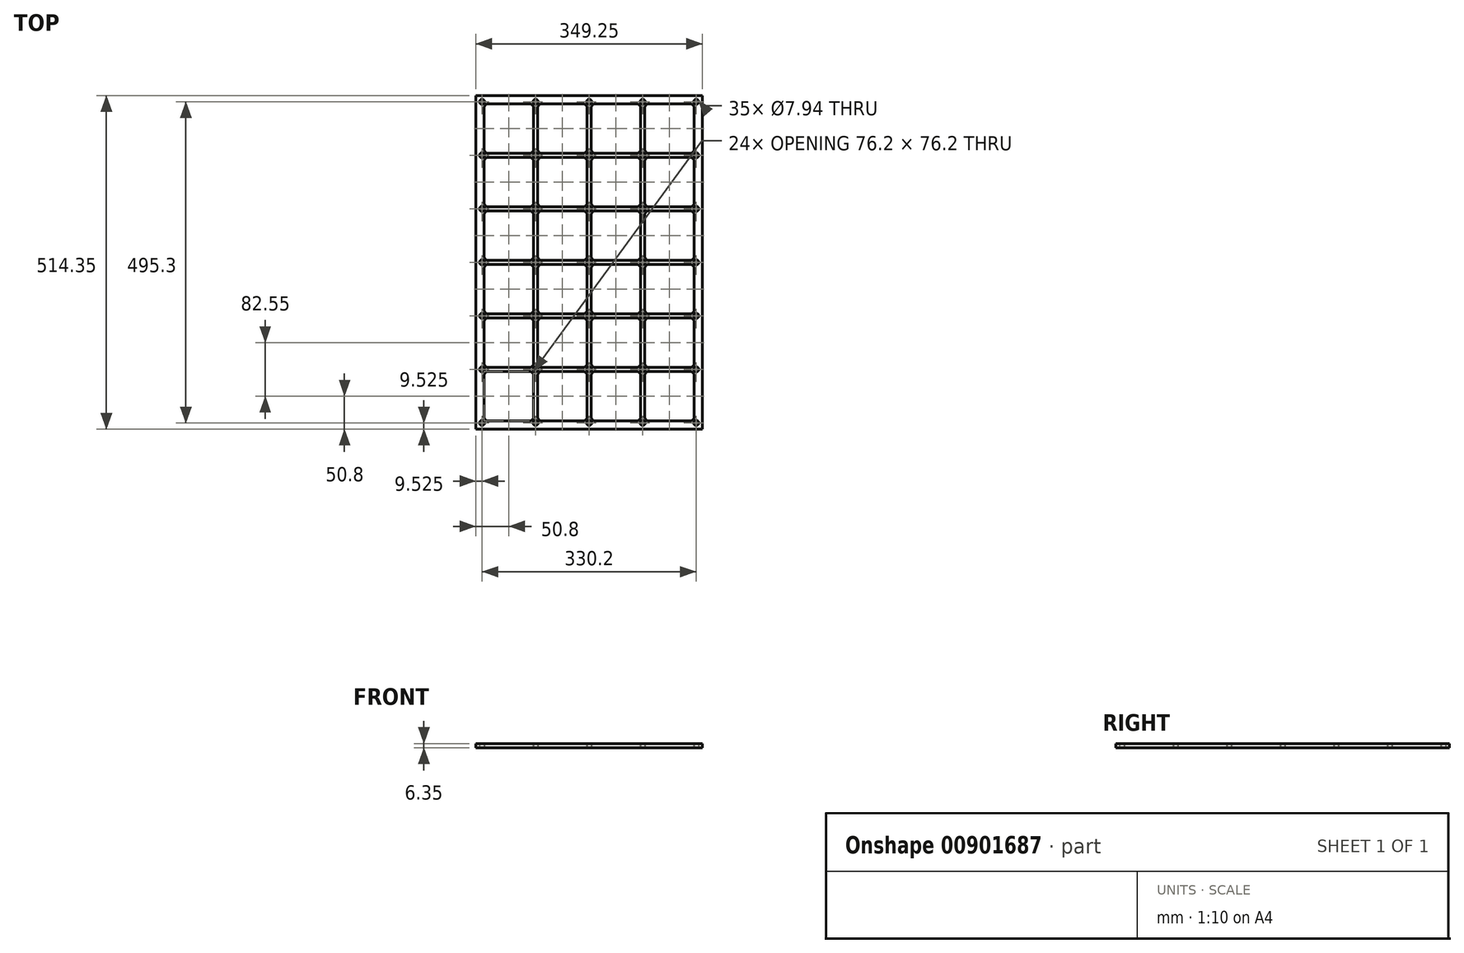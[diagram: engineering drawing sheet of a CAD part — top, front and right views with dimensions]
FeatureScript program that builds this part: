
annotation { "Feature Type Name" : "Feature", "Feature Type Description" : "" }
export const myFeature = defineFeature(function(context is Context, id is Id, definition is map)
    precondition{}
    {
        {
            var Q0;
            Q0=qCreatedBy(makeId("Top.planeOp"),FACE);
            var sketch = newSketch(context, id + "F0", { "sketchPlane" : qUnion([Q0])});
            skLineSegment(sketch, "E0.bottom", {"start": v(0, 0) * mm, "end": v(349.25, 0) * mm});
            skLineSegment(sketch, "E0.top", {"start": v(0, 514.35) * mm, "end": v(349.25, 514.35) * mm});
            skLineSegment(sketch, "E0.left", {"start": v(0, 0) * mm, "end": v(0, 514.35) * mm});
            skLineSegment(sketch, "E0.right", {"start": v(349.25, 0) * mm, "end": v(349.25, 514.35) * mm});
            skLineSegment(sketch, "E1.bottom", {"start": v(19.05, 12.7) * mm, "end": v(82.55, 12.7) * mm});
            skLineSegment(sketch, "E1.top", {"start": v(19.05, 88.9) * mm, "end": v(82.55, 88.9) * mm});
            skLineSegment(sketch, "E1.left", {"start": v(12.7, 19.05) * mm, "end": v(12.7, 82.55) * mm});
            skLineSegment(sketch, "E1.right", {"start": v(88.9, 19.05) * mm, "end": v(88.9, 82.55) * mm});
            skArc(sketch, "E2.filletArc", {"start": v(19.05, 88.9) * mm, "mid": v(14.56, 87.04) * mm, "end": v(12.7, 82.55) * mm});
            skArc(sketch, "E3.filletArc", {"start": v(88.9, 82.55) * mm, "mid": v(87.04, 87.04) * mm, "end": v(82.55, 88.9) * mm});
            skArc(sketch, "E4.filletArc", {"start": v(82.55, 12.7) * mm, "mid": v(87.04, 14.56) * mm, "end": v(88.9, 19.05) * mm});
            skArc(sketch, "E5.filletArc", {"start": v(12.7, 19.05) * mm, "mid": v(14.56, 14.56) * mm, "end": v(19.05, 12.7) * mm});
            skLineSegment(sketch, "E6.0.1.0", {"start": v(19.05, 171.45) * mm, "end": v(82.55, 171.45) * mm});
            skLineSegment(sketch, "E6.0.1.1", {"start": v(88.9, 101.6) * mm, "end": v(88.9, 165.1) * mm});
            skArc(sketch, "E6.0.1.2", {"start": v(88.9, 165.1) * mm, "mid": v(87.04, 169.6) * mm, "end": v(82.55, 171.45) * mm});
            skArc(sketch, "E6.0.1.3", {"start": v(82.55, 95.25) * mm, "mid": v(87.04, 97.1) * mm, "end": v(88.9, 101.6) * mm});
            skLineSegment(sketch, "E6.0.1.4", {"start": v(19.05, 95.25) * mm, "end": v(82.55, 95.25) * mm});
            skArc(sketch, "E6.0.1.5", {"start": v(12.7, 101.6) * mm, "mid": v(14.56, 97.1) * mm, "end": v(19.05, 95.25) * mm});
            skLineSegment(sketch, "E6.0.1.6", {"start": v(12.7, 101.6) * mm, "end": v(12.7, 165.1) * mm});
            skArc(sketch, "E6.0.1.7", {"start": v(19.05, 171.45) * mm, "mid": v(14.56, 169.6) * mm, "end": v(12.7, 165.1) * mm});
            skLineSegment(sketch, "E6.0.2.0", {"start": v(19.05, 254) * mm, "end": v(82.55, 254) * mm});
            skLineSegment(sketch, "E6.0.2.1", {"start": v(88.9, 184.15) * mm, "end": v(88.9, 247.65) * mm});
            skArc(sketch, "E6.0.2.2", {"start": v(88.9, 247.65) * mm, "mid": v(87.04, 252.14) * mm, "end": v(82.55, 254) * mm});
            skArc(sketch, "E6.0.2.3", {"start": v(82.55, 177.8) * mm, "mid": v(87.04, 179.66) * mm, "end": v(88.9, 184.15) * mm});
            skLineSegment(sketch, "E6.0.2.4", {"start": v(19.05, 177.8) * mm, "end": v(82.55, 177.8) * mm});
            skArc(sketch, "E6.0.2.5", {"start": v(12.7, 184.15) * mm, "mid": v(14.56, 179.66) * mm, "end": v(19.05, 177.8) * mm});
            skLineSegment(sketch, "E6.0.2.6", {"start": v(12.7, 184.15) * mm, "end": v(12.7, 247.65) * mm});
            skArc(sketch, "E6.0.2.7", {"start": v(19.05, 254) * mm, "mid": v(14.56, 252.14) * mm, "end": v(12.7, 247.65) * mm});
            skLineSegment(sketch, "E6.0.3.0", {"start": v(19.05, 336.55) * mm, "end": v(82.55, 336.55) * mm});
            skLineSegment(sketch, "E6.0.3.1", {"start": v(88.9, 266.7) * mm, "end": v(88.9, 330.2) * mm});
            skArc(sketch, "E6.0.3.2", {"start": v(88.9, 330.2) * mm, "mid": v(87.04, 334.7) * mm, "end": v(82.55, 336.55) * mm});
            skArc(sketch, "E6.0.3.3", {"start": v(82.55, 260.35) * mm, "mid": v(87.04, 262.2) * mm, "end": v(88.9, 266.7) * mm});
            skLineSegment(sketch, "E6.0.3.4", {"start": v(19.05, 260.35) * mm, "end": v(82.55, 260.35) * mm});
            skArc(sketch, "E6.0.3.5", {"start": v(12.7, 266.7) * mm, "mid": v(14.56, 262.2) * mm, "end": v(19.05, 260.35) * mm});
            skLineSegment(sketch, "E6.0.3.6", {"start": v(12.7, 266.7) * mm, "end": v(12.7, 330.2) * mm});
            skArc(sketch, "E6.0.3.7", {"start": v(19.05, 336.55) * mm, "mid": v(14.56, 334.7) * mm, "end": v(12.7, 330.2) * mm});
            skLineSegment(sketch, "E6.0.4.0", {"start": v(19.05, 419.1) * mm, "end": v(82.55, 419.1) * mm});
            skLineSegment(sketch, "E6.0.4.1", {"start": v(88.9, 349.25) * mm, "end": v(88.9, 412.75) * mm});
            skArc(sketch, "E6.0.4.2", {"start": v(88.9, 412.75) * mm, "mid": v(87.04, 417.24) * mm, "end": v(82.55, 419.1) * mm});
            skArc(sketch, "E6.0.4.3", {"start": v(82.55, 342.9) * mm, "mid": v(87.04, 344.76) * mm, "end": v(88.9, 349.25) * mm});
            skLineSegment(sketch, "E6.0.4.4", {"start": v(19.05, 342.9) * mm, "end": v(82.55, 342.9) * mm});
            skArc(sketch, "E6.0.4.5", {"start": v(12.7, 349.25) * mm, "mid": v(14.56, 344.76) * mm, "end": v(19.05, 342.9) * mm});
            skLineSegment(sketch, "E6.0.4.6", {"start": v(12.7, 349.25) * mm, "end": v(12.7, 412.75) * mm});
            skArc(sketch, "E6.0.4.7", {"start": v(19.05, 419.1) * mm, "mid": v(14.56, 417.24) * mm, "end": v(12.7, 412.75) * mm});
            skLineSegment(sketch, "E6.0.5.0", {"start": v(19.05, 501.65) * mm, "end": v(82.55, 501.65) * mm});
            skLineSegment(sketch, "E6.0.5.1", {"start": v(88.9, 431.8) * mm, "end": v(88.9, 495.3) * mm});
            skArc(sketch, "E6.0.5.2", {"start": v(88.9, 495.3) * mm, "mid": v(87.04, 499.8) * mm, "end": v(82.55, 501.65) * mm});
            skArc(sketch, "E6.0.5.3", {"start": v(82.55, 425.45) * mm, "mid": v(87.04, 427.3) * mm, "end": v(88.9, 431.8) * mm});
            skLineSegment(sketch, "E6.0.5.4", {"start": v(19.05, 425.45) * mm, "end": v(82.55, 425.45) * mm});
            skArc(sketch, "E6.0.5.5", {"start": v(12.7, 431.8) * mm, "mid": v(14.56, 427.3) * mm, "end": v(19.05, 425.45) * mm});
            skLineSegment(sketch, "E6.0.5.6", {"start": v(12.7, 431.8) * mm, "end": v(12.7, 495.3) * mm});
            skArc(sketch, "E6.0.5.7", {"start": v(19.05, 501.65) * mm, "mid": v(14.56, 499.8) * mm, "end": v(12.7, 495.3) * mm});
            skLineSegment(sketch, "E6.1.0.0", {"start": v(101.6, 88.9) * mm, "end": v(165.1, 88.9) * mm});
            skLineSegment(sketch, "E6.1.0.1", {"start": v(171.45, 19.05) * mm, "end": v(171.45, 82.55) * mm});
            skArc(sketch, "E6.1.0.2", {"start": v(171.45, 82.55) * mm, "mid": v(169.6, 87.04) * mm, "end": v(165.1, 88.9) * mm});
            skArc(sketch, "E6.1.0.3", {"start": v(165.1, 12.7) * mm, "mid": v(169.6, 14.56) * mm, "end": v(171.45, 19.05) * mm});
            skLineSegment(sketch, "E6.1.0.4", {"start": v(101.6, 12.7) * mm, "end": v(165.1, 12.7) * mm});
            skArc(sketch, "E6.1.0.5", {"start": v(95.25, 19.05) * mm, "mid": v(97.1, 14.56) * mm, "end": v(101.6, 12.7) * mm});
            skLineSegment(sketch, "E6.1.0.6", {"start": v(95.25, 19.05) * mm, "end": v(95.25, 82.55) * mm});
            skArc(sketch, "E6.1.0.7", {"start": v(101.6, 88.9) * mm, "mid": v(97.1, 87.04) * mm, "end": v(95.25, 82.55) * mm});
            skLineSegment(sketch, "E6.1.1.0", {"start": v(101.6, 171.45) * mm, "end": v(165.1, 171.45) * mm});
            skLineSegment(sketch, "E6.1.1.1", {"start": v(171.45, 101.6) * mm, "end": v(171.45, 165.1) * mm});
            skArc(sketch, "E6.1.1.2", {"start": v(171.45, 165.1) * mm, "mid": v(169.6, 169.6) * mm, "end": v(165.1, 171.45) * mm});
            skArc(sketch, "E6.1.1.3", {"start": v(165.1, 95.25) * mm, "mid": v(169.6, 97.1) * mm, "end": v(171.45, 101.6) * mm});
            skLineSegment(sketch, "E6.1.1.4", {"start": v(101.6, 95.25) * mm, "end": v(165.1, 95.25) * mm});
            skArc(sketch, "E6.1.1.5", {"start": v(95.25, 101.6) * mm, "mid": v(97.1, 97.1) * mm, "end": v(101.6, 95.25) * mm});
            skLineSegment(sketch, "E6.1.1.6", {"start": v(95.25, 101.6) * mm, "end": v(95.25, 165.1) * mm});
            skArc(sketch, "E6.1.1.7", {"start": v(101.6, 171.45) * mm, "mid": v(97.1, 169.6) * mm, "end": v(95.25, 165.1) * mm});
            skLineSegment(sketch, "E6.1.2.0", {"start": v(101.6, 254) * mm, "end": v(165.1, 254) * mm});
            skLineSegment(sketch, "E6.1.2.1", {"start": v(171.45, 184.15) * mm, "end": v(171.45, 247.65) * mm});
            skArc(sketch, "E6.1.2.2", {"start": v(171.45, 247.65) * mm, "mid": v(169.6, 252.14) * mm, "end": v(165.1, 254) * mm});
            skArc(sketch, "E6.1.2.3", {"start": v(165.1, 177.8) * mm, "mid": v(169.6, 179.66) * mm, "end": v(171.45, 184.15) * mm});
            skLineSegment(sketch, "E6.1.2.4", {"start": v(101.6, 177.8) * mm, "end": v(165.1, 177.8) * mm});
            skArc(sketch, "E6.1.2.5", {"start": v(95.25, 184.15) * mm, "mid": v(97.1, 179.66) * mm, "end": v(101.6, 177.8) * mm});
            skLineSegment(sketch, "E6.1.2.6", {"start": v(95.25, 184.15) * mm, "end": v(95.25, 247.65) * mm});
            skArc(sketch, "E6.1.2.7", {"start": v(101.6, 254) * mm, "mid": v(97.1, 252.14) * mm, "end": v(95.25, 247.65) * mm});
            skLineSegment(sketch, "E6.1.3.0", {"start": v(101.6, 336.55) * mm, "end": v(165.1, 336.55) * mm});
            skLineSegment(sketch, "E6.1.3.1", {"start": v(171.45, 266.7) * mm, "end": v(171.45, 330.2) * mm});
            skArc(sketch, "E6.1.3.2", {"start": v(171.45, 330.2) * mm, "mid": v(169.6, 334.7) * mm, "end": v(165.1, 336.55) * mm});
            skArc(sketch, "E6.1.3.3", {"start": v(165.1, 260.35) * mm, "mid": v(169.6, 262.2) * mm, "end": v(171.45, 266.7) * mm});
            skLineSegment(sketch, "E6.1.3.4", {"start": v(101.6, 260.35) * mm, "end": v(165.1, 260.35) * mm});
            skArc(sketch, "E6.1.3.5", {"start": v(95.25, 266.7) * mm, "mid": v(97.1, 262.2) * mm, "end": v(101.6, 260.35) * mm});
            skLineSegment(sketch, "E6.1.3.6", {"start": v(95.25, 266.7) * mm, "end": v(95.25, 330.2) * mm});
            skArc(sketch, "E6.1.3.7", {"start": v(101.6, 336.55) * mm, "mid": v(97.1, 334.7) * mm, "end": v(95.25, 330.2) * mm});
            skLineSegment(sketch, "E6.1.4.0", {"start": v(101.6, 419.1) * mm, "end": v(165.1, 419.1) * mm});
            skLineSegment(sketch, "E6.1.4.1", {"start": v(171.45, 349.25) * mm, "end": v(171.45, 412.75) * mm});
            skArc(sketch, "E6.1.4.2", {"start": v(171.45, 412.75) * mm, "mid": v(169.6, 417.24) * mm, "end": v(165.1, 419.1) * mm});
            skArc(sketch, "E6.1.4.3", {"start": v(165.1, 342.9) * mm, "mid": v(169.6, 344.76) * mm, "end": v(171.45, 349.25) * mm});
            skLineSegment(sketch, "E6.1.4.4", {"start": v(101.6, 342.9) * mm, "end": v(165.1, 342.9) * mm});
            skArc(sketch, "E6.1.4.5", {"start": v(95.25, 349.25) * mm, "mid": v(97.1, 344.76) * mm, "end": v(101.6, 342.9) * mm});
            skLineSegment(sketch, "E6.1.4.6", {"start": v(95.25, 349.25) * mm, "end": v(95.25, 412.75) * mm});
            skArc(sketch, "E6.1.4.7", {"start": v(101.6, 419.1) * mm, "mid": v(97.1, 417.24) * mm, "end": v(95.25, 412.75) * mm});
            skLineSegment(sketch, "E6.1.5.0", {"start": v(101.6, 501.65) * mm, "end": v(165.1, 501.65) * mm});
            skLineSegment(sketch, "E6.1.5.1", {"start": v(171.45, 431.8) * mm, "end": v(171.45, 495.3) * mm});
            skArc(sketch, "E6.1.5.2", {"start": v(171.45, 495.3) * mm, "mid": v(169.6, 499.8) * mm, "end": v(165.1, 501.65) * mm});
            skArc(sketch, "E6.1.5.3", {"start": v(165.1, 425.45) * mm, "mid": v(169.6, 427.3) * mm, "end": v(171.45, 431.8) * mm});
            skLineSegment(sketch, "E6.1.5.4", {"start": v(101.6, 425.45) * mm, "end": v(165.1, 425.45) * mm});
            skArc(sketch, "E6.1.5.5", {"start": v(95.25, 431.8) * mm, "mid": v(97.1, 427.3) * mm, "end": v(101.6, 425.45) * mm});
            skLineSegment(sketch, "E6.1.5.6", {"start": v(95.25, 431.8) * mm, "end": v(95.25, 495.3) * mm});
            skArc(sketch, "E6.1.5.7", {"start": v(101.6, 501.65) * mm, "mid": v(97.1, 499.8) * mm, "end": v(95.25, 495.3) * mm});
            skLineSegment(sketch, "E6.2.0.0", {"start": v(184.15, 88.9) * mm, "end": v(247.65, 88.9) * mm});
            skLineSegment(sketch, "E6.2.0.1", {"start": v(254, 19.05) * mm, "end": v(254, 82.55) * mm});
            skArc(sketch, "E6.2.0.2", {"start": v(254, 82.55) * mm, "mid": v(252.14, 87.04) * mm, "end": v(247.65, 88.9) * mm});
            skArc(sketch, "E6.2.0.3", {"start": v(247.65, 12.7) * mm, "mid": v(252.14, 14.56) * mm, "end": v(254, 19.05) * mm});
            skLineSegment(sketch, "E6.2.0.4", {"start": v(184.15, 12.7) * mm, "end": v(247.65, 12.7) * mm});
            skArc(sketch, "E6.2.0.5", {"start": v(177.8, 19.05) * mm, "mid": v(179.66, 14.56) * mm, "end": v(184.15, 12.7) * mm});
            skLineSegment(sketch, "E6.2.0.6", {"start": v(177.8, 19.05) * mm, "end": v(177.8, 82.55) * mm});
            skArc(sketch, "E6.2.0.7", {"start": v(184.15, 88.9) * mm, "mid": v(179.66, 87.04) * mm, "end": v(177.8, 82.55) * mm});
            skLineSegment(sketch, "E6.2.1.0", {"start": v(184.15, 171.45) * mm, "end": v(247.65, 171.45) * mm});
            skLineSegment(sketch, "E6.2.1.1", {"start": v(254, 101.6) * mm, "end": v(254, 165.1) * mm});
            skArc(sketch, "E6.2.1.2", {"start": v(254, 165.1) * mm, "mid": v(252.14, 169.6) * mm, "end": v(247.65, 171.45) * mm});
            skArc(sketch, "E6.2.1.3", {"start": v(247.65, 95.25) * mm, "mid": v(252.14, 97.1) * mm, "end": v(254, 101.6) * mm});
            skLineSegment(sketch, "E6.2.1.4", {"start": v(184.15, 95.25) * mm, "end": v(247.65, 95.25) * mm});
            skArc(sketch, "E6.2.1.5", {"start": v(177.8, 101.6) * mm, "mid": v(179.66, 97.1) * mm, "end": v(184.15, 95.25) * mm});
            skLineSegment(sketch, "E6.2.1.6", {"start": v(177.8, 101.6) * mm, "end": v(177.8, 165.1) * mm});
            skArc(sketch, "E6.2.1.7", {"start": v(184.15, 171.45) * mm, "mid": v(179.66, 169.6) * mm, "end": v(177.8, 165.1) * mm});
            skLineSegment(sketch, "E6.2.2.0", {"start": v(184.15, 254) * mm, "end": v(247.65, 254) * mm});
            skLineSegment(sketch, "E6.2.2.1", {"start": v(254, 184.15) * mm, "end": v(254, 247.65) * mm});
            skArc(sketch, "E6.2.2.2", {"start": v(254, 247.65) * mm, "mid": v(252.14, 252.14) * mm, "end": v(247.65, 254) * mm});
            skArc(sketch, "E6.2.2.3", {"start": v(247.65, 177.8) * mm, "mid": v(252.14, 179.66) * mm, "end": v(254, 184.15) * mm});
            skLineSegment(sketch, "E6.2.2.4", {"start": v(184.15, 177.8) * mm, "end": v(247.65, 177.8) * mm});
            skArc(sketch, "E6.2.2.5", {"start": v(177.8, 184.15) * mm, "mid": v(179.66, 179.66) * mm, "end": v(184.15, 177.8) * mm});
            skLineSegment(sketch, "E6.2.2.6", {"start": v(177.8, 184.15) * mm, "end": v(177.8, 247.65) * mm});
            skArc(sketch, "E6.2.2.7", {"start": v(184.15, 254) * mm, "mid": v(179.66, 252.14) * mm, "end": v(177.8, 247.65) * mm});
            skLineSegment(sketch, "E6.2.3.0", {"start": v(184.15, 336.55) * mm, "end": v(247.65, 336.55) * mm});
            skLineSegment(sketch, "E6.2.3.1", {"start": v(254, 266.7) * mm, "end": v(254, 330.2) * mm});
            skArc(sketch, "E6.2.3.2", {"start": v(254, 330.2) * mm, "mid": v(252.14, 334.7) * mm, "end": v(247.65, 336.55) * mm});
            skArc(sketch, "E6.2.3.3", {"start": v(247.65, 260.35) * mm, "mid": v(252.14, 262.2) * mm, "end": v(254, 266.7) * mm});
            skLineSegment(sketch, "E6.2.3.4", {"start": v(184.15, 260.35) * mm, "end": v(247.65, 260.35) * mm});
            skArc(sketch, "E6.2.3.5", {"start": v(177.8, 266.7) * mm, "mid": v(179.66, 262.2) * mm, "end": v(184.15, 260.35) * mm});
            skLineSegment(sketch, "E6.2.3.6", {"start": v(177.8, 266.7) * mm, "end": v(177.8, 330.2) * mm});
            skArc(sketch, "E6.2.3.7", {"start": v(184.15, 336.55) * mm, "mid": v(179.66, 334.7) * mm, "end": v(177.8, 330.2) * mm});
            skLineSegment(sketch, "E6.2.4.0", {"start": v(184.15, 419.1) * mm, "end": v(247.65, 419.1) * mm});
            skLineSegment(sketch, "E6.2.4.1", {"start": v(254, 349.25) * mm, "end": v(254, 412.75) * mm});
            skArc(sketch, "E6.2.4.2", {"start": v(254, 412.75) * mm, "mid": v(252.14, 417.24) * mm, "end": v(247.65, 419.1) * mm});
            skArc(sketch, "E6.2.4.3", {"start": v(247.65, 342.9) * mm, "mid": v(252.14, 344.76) * mm, "end": v(254, 349.25) * mm});
            skLineSegment(sketch, "E6.2.4.4", {"start": v(184.15, 342.9) * mm, "end": v(247.65, 342.9) * mm});
            skArc(sketch, "E6.2.4.5", {"start": v(177.8, 349.25) * mm, "mid": v(179.66, 344.76) * mm, "end": v(184.15, 342.9) * mm});
            skLineSegment(sketch, "E6.2.4.6", {"start": v(177.8, 349.25) * mm, "end": v(177.8, 412.75) * mm});
            skArc(sketch, "E6.2.4.7", {"start": v(184.15, 419.1) * mm, "mid": v(179.66, 417.24) * mm, "end": v(177.8, 412.75) * mm});
            skLineSegment(sketch, "E6.2.5.0", {"start": v(184.15, 501.65) * mm, "end": v(247.65, 501.65) * mm});
            skLineSegment(sketch, "E6.2.5.1", {"start": v(254, 431.8) * mm, "end": v(254, 495.3) * mm});
            skArc(sketch, "E6.2.5.2", {"start": v(254, 495.3) * mm, "mid": v(252.14, 499.8) * mm, "end": v(247.65, 501.65) * mm});
            skArc(sketch, "E6.2.5.3", {"start": v(247.65, 425.45) * mm, "mid": v(252.14, 427.3) * mm, "end": v(254, 431.8) * mm});
            skLineSegment(sketch, "E6.2.5.4", {"start": v(184.15, 425.45) * mm, "end": v(247.65, 425.45) * mm});
            skArc(sketch, "E6.2.5.5", {"start": v(177.8, 431.8) * mm, "mid": v(179.66, 427.3) * mm, "end": v(184.15, 425.45) * mm});
            skLineSegment(sketch, "E6.2.5.6", {"start": v(177.8, 431.8) * mm, "end": v(177.8, 495.3) * mm});
            skArc(sketch, "E6.2.5.7", {"start": v(184.15, 501.65) * mm, "mid": v(179.66, 499.8) * mm, "end": v(177.8, 495.3) * mm});
            skLineSegment(sketch, "E6.3.0.0", {"start": v(266.7, 88.9) * mm, "end": v(330.2, 88.9) * mm});
            skLineSegment(sketch, "E6.3.0.1", {"start": v(336.55, 19.05) * mm, "end": v(336.55, 82.55) * mm});
            skArc(sketch, "E6.3.0.2", {"start": v(336.55, 82.55) * mm, "mid": v(334.7, 87.04) * mm, "end": v(330.2, 88.9) * mm});
            skArc(sketch, "E6.3.0.3", {"start": v(330.2, 12.7) * mm, "mid": v(334.7, 14.56) * mm, "end": v(336.55, 19.05) * mm});
            skLineSegment(sketch, "E6.3.0.4", {"start": v(266.7, 12.7) * mm, "end": v(330.2, 12.7) * mm});
            skArc(sketch, "E6.3.0.5", {"start": v(260.35, 19.05) * mm, "mid": v(262.2, 14.56) * mm, "end": v(266.7, 12.7) * mm});
            skLineSegment(sketch, "E6.3.0.6", {"start": v(260.35, 19.05) * mm, "end": v(260.35, 82.55) * mm});
            skArc(sketch, "E6.3.0.7", {"start": v(266.7, 88.9) * mm, "mid": v(262.2, 87.04) * mm, "end": v(260.35, 82.55) * mm});
            skLineSegment(sketch, "E6.3.1.0", {"start": v(266.7, 171.45) * mm, "end": v(330.2, 171.45) * mm});
            skLineSegment(sketch, "E6.3.1.1", {"start": v(336.55, 101.6) * mm, "end": v(336.55, 165.1) * mm});
            skArc(sketch, "E6.3.1.2", {"start": v(336.55, 165.1) * mm, "mid": v(334.7, 169.6) * mm, "end": v(330.2, 171.45) * mm});
            skArc(sketch, "E6.3.1.3", {"start": v(330.2, 95.25) * mm, "mid": v(334.7, 97.1) * mm, "end": v(336.55, 101.6) * mm});
            skLineSegment(sketch, "E6.3.1.4", {"start": v(266.7, 95.25) * mm, "end": v(330.2, 95.25) * mm});
            skArc(sketch, "E6.3.1.5", {"start": v(260.35, 101.6) * mm, "mid": v(262.2, 97.1) * mm, "end": v(266.7, 95.25) * mm});
            skLineSegment(sketch, "E6.3.1.6", {"start": v(260.35, 101.6) * mm, "end": v(260.35, 165.1) * mm});
            skArc(sketch, "E6.3.1.7", {"start": v(266.7, 171.45) * mm, "mid": v(262.2, 169.6) * mm, "end": v(260.35, 165.1) * mm});
            skLineSegment(sketch, "E6.3.2.0", {"start": v(266.7, 254) * mm, "end": v(330.2, 254) * mm});
            skLineSegment(sketch, "E6.3.2.1", {"start": v(336.55, 184.15) * mm, "end": v(336.55, 247.65) * mm});
            skArc(sketch, "E6.3.2.2", {"start": v(336.55, 247.65) * mm, "mid": v(334.7, 252.14) * mm, "end": v(330.2, 254) * mm});
            skArc(sketch, "E6.3.2.3", {"start": v(330.2, 177.8) * mm, "mid": v(334.7, 179.66) * mm, "end": v(336.55, 184.15) * mm});
            skLineSegment(sketch, "E6.3.2.4", {"start": v(266.7, 177.8) * mm, "end": v(330.2, 177.8) * mm});
            skArc(sketch, "E6.3.2.5", {"start": v(260.35, 184.15) * mm, "mid": v(262.2, 179.66) * mm, "end": v(266.7, 177.8) * mm});
            skLineSegment(sketch, "E6.3.2.6", {"start": v(260.35, 184.15) * mm, "end": v(260.35, 247.65) * mm});
            skArc(sketch, "E6.3.2.7", {"start": v(266.7, 254) * mm, "mid": v(262.2, 252.14) * mm, "end": v(260.35, 247.65) * mm});
            skLineSegment(sketch, "E6.3.3.0", {"start": v(266.7, 336.55) * mm, "end": v(330.2, 336.55) * mm});
            skLineSegment(sketch, "E6.3.3.1", {"start": v(336.55, 266.7) * mm, "end": v(336.55, 330.2) * mm});
            skArc(sketch, "E6.3.3.2", {"start": v(336.55, 330.2) * mm, "mid": v(334.7, 334.7) * mm, "end": v(330.2, 336.55) * mm});
            skArc(sketch, "E6.3.3.3", {"start": v(330.2, 260.35) * mm, "mid": v(334.7, 262.2) * mm, "end": v(336.55, 266.7) * mm});
            skLineSegment(sketch, "E6.3.3.4", {"start": v(266.7, 260.35) * mm, "end": v(330.2, 260.35) * mm});
            skArc(sketch, "E6.3.3.5", {"start": v(260.35, 266.7) * mm, "mid": v(262.2, 262.2) * mm, "end": v(266.7, 260.35) * mm});
            skLineSegment(sketch, "E6.3.3.6", {"start": v(260.35, 266.7) * mm, "end": v(260.35, 330.2) * mm});
            skArc(sketch, "E6.3.3.7", {"start": v(266.7, 336.55) * mm, "mid": v(262.2, 334.7) * mm, "end": v(260.35, 330.2) * mm});
            skLineSegment(sketch, "E6.3.4.0", {"start": v(266.7, 419.1) * mm, "end": v(330.2, 419.1) * mm});
            skLineSegment(sketch, "E6.3.4.1", {"start": v(336.55, 349.25) * mm, "end": v(336.55, 412.75) * mm});
            skArc(sketch, "E6.3.4.2", {"start": v(336.55, 412.75) * mm, "mid": v(334.7, 417.24) * mm, "end": v(330.2, 419.1) * mm});
            skArc(sketch, "E6.3.4.3", {"start": v(330.2, 342.9) * mm, "mid": v(334.7, 344.76) * mm, "end": v(336.55, 349.25) * mm});
            skLineSegment(sketch, "E6.3.4.4", {"start": v(266.7, 342.9) * mm, "end": v(330.2, 342.9) * mm});
            skArc(sketch, "E6.3.4.5", {"start": v(260.35, 349.25) * mm, "mid": v(262.2, 344.76) * mm, "end": v(266.7, 342.9) * mm});
            skLineSegment(sketch, "E6.3.4.6", {"start": v(260.35, 349.25) * mm, "end": v(260.35, 412.75) * mm});
            skArc(sketch, "E6.3.4.7", {"start": v(266.7, 419.1) * mm, "mid": v(262.2, 417.24) * mm, "end": v(260.35, 412.75) * mm});
            skLineSegment(sketch, "E6.3.5.0", {"start": v(266.7, 501.65) * mm, "end": v(330.2, 501.65) * mm});
            skLineSegment(sketch, "E6.3.5.1", {"start": v(336.55, 431.8) * mm, "end": v(336.55, 495.3) * mm});
            skArc(sketch, "E6.3.5.2", {"start": v(336.55, 495.3) * mm, "mid": v(334.7, 499.8) * mm, "end": v(330.2, 501.65) * mm});
            skArc(sketch, "E6.3.5.3", {"start": v(330.2, 425.45) * mm, "mid": v(334.7, 427.3) * mm, "end": v(336.55, 431.8) * mm});
            skLineSegment(sketch, "E6.3.5.4", {"start": v(266.7, 425.45) * mm, "end": v(330.2, 425.45) * mm});
            skArc(sketch, "E6.3.5.5", {"start": v(260.35, 431.8) * mm, "mid": v(262.2, 427.3) * mm, "end": v(266.7, 425.45) * mm});
            skLineSegment(sketch, "E6.3.5.6", {"start": v(260.35, 431.8) * mm, "end": v(260.35, 495.3) * mm});
            skArc(sketch, "E6.3.5.7", {"start": v(266.7, 501.65) * mm, "mid": v(262.2, 499.8) * mm, "end": v(260.35, 495.3) * mm});
            skLineSegment(sketch, "E6.direction1", {"start": v(19.05, 12.7) * mm, "end": v(101.6, 12.7) * mm, "construction": true});
            skLineSegment(sketch, "E6.direction2", {"start": v(19.05, 12.7) * mm, "end": v(19.05, 95.25) * mm, "construction": true});
            skLineSegment(sketch, "E7", {"start": v(165.1, 101.6) * mm, "end": v(184.15, 82.55) * mm, "construction": true});
            skLineSegment(sketch, "E8", {"start": v(266.7, 101.6) * mm, "end": v(247.65, 82.55) * mm, "construction": true});
            skLineSegment(sketch, "E9", {"start": v(247.65, 184.15) * mm, "end": v(266.7, 165.1) * mm, "construction": true});
            skLineSegment(sketch, "E10", {"start": v(184.15, 184.15) * mm, "end": v(165.1, 165.1) * mm, "construction": true});
            skLineSegment(sketch, "E11", {"start": v(174.63, 174.63) * mm, "end": v(174.63, 92.08) * mm, "construction": true});
            skLineSegment(sketch, "E12", {"start": v(174.63, 92.08) * mm, "end": v(257.18, 92.08) * mm, "construction": true});
            skCircle(sketch, "E13", {"center": v(9.53, 9.53) * mm, "radius": 3.97 * mm});
            skCircle(sketch, "E14.0.1.0", {"center": v(9.53, 92.08) * mm, "radius": 3.97 * mm});
            skCircle(sketch, "E14.0.2.0", {"center": v(9.53, 174.63) * mm, "radius": 3.97 * mm});
            skCircle(sketch, "E14.0.3.0", {"center": v(9.53, 257.18) * mm, "radius": 3.97 * mm});
            skCircle(sketch, "E14.0.4.0", {"center": v(9.53, 339.73) * mm, "radius": 3.97 * mm});
            skCircle(sketch, "E14.0.5.0", {"center": v(9.53, 422.28) * mm, "radius": 3.97 * mm});
            skCircle(sketch, "E14.0.6.0", {"center": v(9.53, 504.83) * mm, "radius": 3.97 * mm});
            skCircle(sketch, "E14.1.0.0", {"center": v(92.08, 9.53) * mm, "radius": 3.97 * mm});
            skCircle(sketch, "E14.1.1.0", {"center": v(92.08, 92.08) * mm, "radius": 3.97 * mm});
            skCircle(sketch, "E14.1.2.0", {"center": v(92.08, 174.63) * mm, "radius": 3.97 * mm});
            skCircle(sketch, "E14.1.3.0", {"center": v(92.08, 257.18) * mm, "radius": 3.97 * mm});
            skCircle(sketch, "E14.1.4.0", {"center": v(92.08, 339.73) * mm, "radius": 3.97 * mm});
            skCircle(sketch, "E14.1.5.0", {"center": v(92.08, 422.28) * mm, "radius": 3.97 * mm});
            skCircle(sketch, "E14.1.6.0", {"center": v(92.08, 504.83) * mm, "radius": 3.97 * mm});
            skCircle(sketch, "E14.2.0.0", {"center": v(174.63, 9.53) * mm, "radius": 3.97 * mm});
            skCircle(sketch, "E14.2.1.0", {"center": v(174.63, 92.08) * mm, "radius": 3.97 * mm});
            skCircle(sketch, "E14.2.2.0", {"center": v(174.63, 174.63) * mm, "radius": 3.97 * mm});
            skCircle(sketch, "E14.2.3.0", {"center": v(174.63, 257.18) * mm, "radius": 3.97 * mm});
            skCircle(sketch, "E14.2.4.0", {"center": v(174.63, 339.73) * mm, "radius": 3.97 * mm});
            skCircle(sketch, "E14.2.5.0", {"center": v(174.63, 422.28) * mm, "radius": 3.97 * mm});
            skCircle(sketch, "E14.2.6.0", {"center": v(174.63, 504.83) * mm, "radius": 3.97 * mm});
            skCircle(sketch, "E14.3.0.0", {"center": v(257.18, 9.53) * mm, "radius": 3.97 * mm});
            skCircle(sketch, "E14.3.1.0", {"center": v(257.18, 92.08) * mm, "radius": 3.97 * mm});
            skCircle(sketch, "E14.3.2.0", {"center": v(257.18, 174.63) * mm, "radius": 3.97 * mm});
            skCircle(sketch, "E14.3.3.0", {"center": v(257.18, 257.18) * mm, "radius": 3.97 * mm});
            skCircle(sketch, "E14.3.4.0", {"center": v(257.18, 339.73) * mm, "radius": 3.97 * mm});
            skCircle(sketch, "E14.3.5.0", {"center": v(257.18, 422.28) * mm, "radius": 3.97 * mm});
            skCircle(sketch, "E14.3.6.0", {"center": v(257.18, 504.83) * mm, "radius": 3.97 * mm});
            skCircle(sketch, "E14.4.0.0", {"center": v(339.73, 9.53) * mm, "radius": 3.97 * mm});
            skCircle(sketch, "E14.4.1.0", {"center": v(339.73, 92.08) * mm, "radius": 3.97 * mm});
            skCircle(sketch, "E14.4.2.0", {"center": v(339.73, 174.63) * mm, "radius": 3.97 * mm});
            skCircle(sketch, "E14.4.3.0", {"center": v(339.73, 257.18) * mm, "radius": 3.97 * mm});
            skCircle(sketch, "E14.4.4.0", {"center": v(339.73, 339.73) * mm, "radius": 3.97 * mm});
            skCircle(sketch, "E14.4.5.0", {"center": v(339.73, 422.28) * mm, "radius": 3.97 * mm});
            skCircle(sketch, "E14.4.6.0", {"center": v(339.73, 504.83) * mm, "radius": 3.97 * mm});
            skLineSegment(sketch, "E14.direction1", {"start": v(9.53, 9.53) * mm, "end": v(92.08, 9.53) * mm, "construction": true});
            skLineSegment(sketch, "E14.direction2", {"start": v(9.53, 9.53) * mm, "end": v(9.53, 92.08) * mm, "construction": true});
            skSolve(sketch);
        }
        {
            var Q0;
            Q0=makeQuery(id+"F0.imprint","IMPRINT",FACE,{"disambiguationData":[TD([[makeQuery(id+"F0.imprint","IMPRINT",EDGE,{"derivedFrom":sQuery(id+"F0.wireOp",EDGE,"E0.bottom")}),1.0]])]});
            extrude(context, id + "F1", {"entities" : qUnion([Q0]), "depth" : 6.35 * mm, "offsetDistance" : 25.4 * mm});
        }
    });
